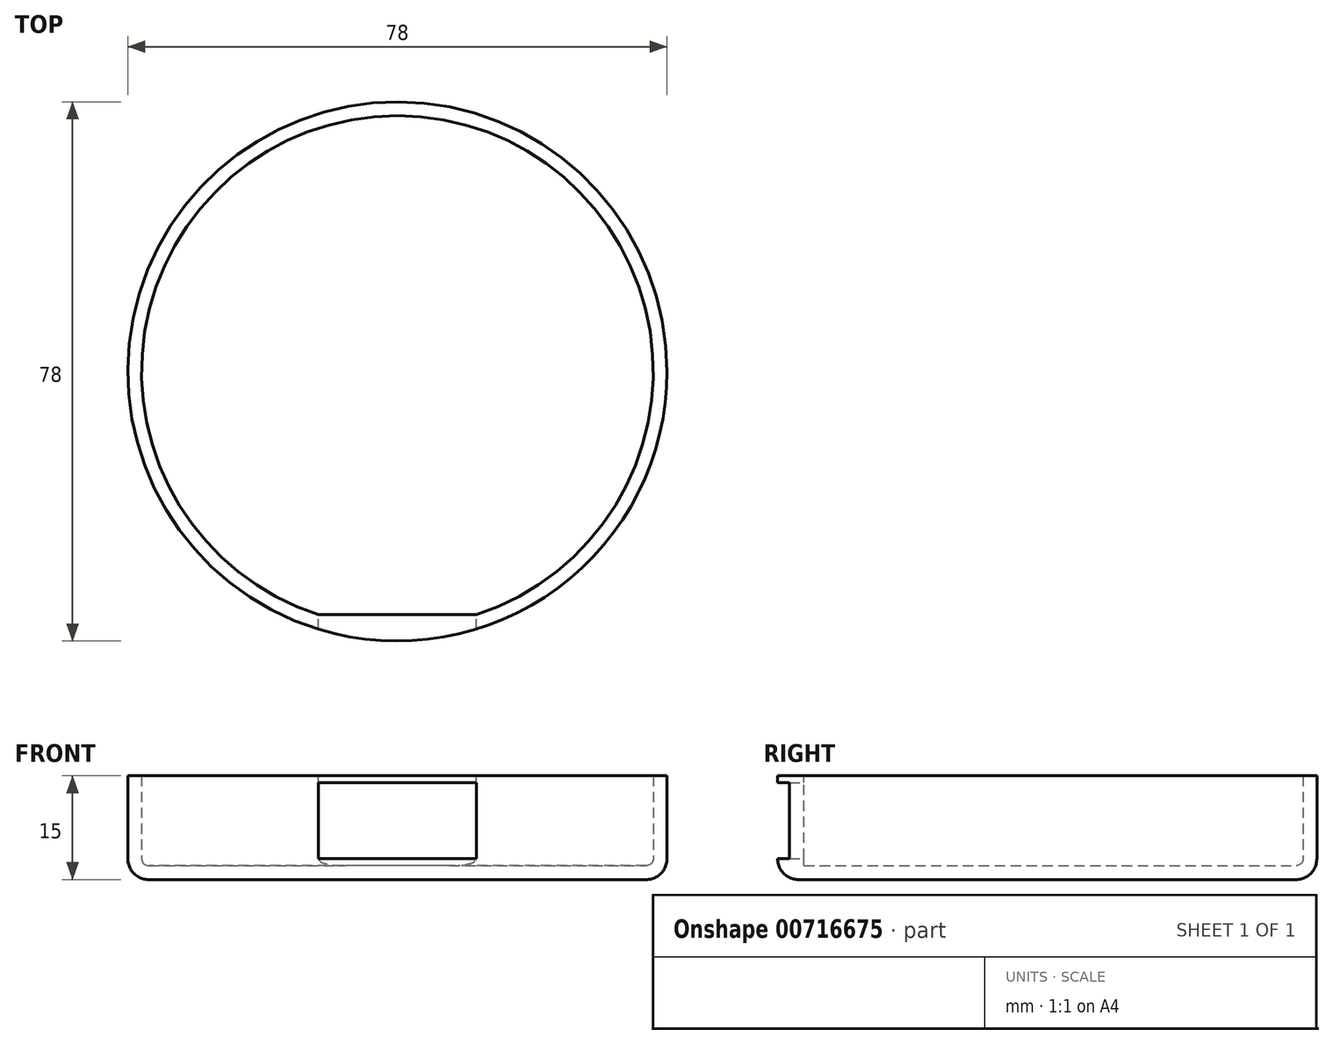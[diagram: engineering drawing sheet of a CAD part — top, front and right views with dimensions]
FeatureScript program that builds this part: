
annotation { "Feature Type Name" : "Feature", "Feature Type Description" : "" }
export const myFeature = defineFeature(function(context is Context, id is Id, definition is map)
    precondition{}
    {
        {
            var Q0;
            Q0=qCreatedBy(makeId("Top.planeOp"),FACE);
            var sketch = newSketch(context, id + "F0", { "sketchPlane" : qUnion([Q0])});
            skCircle(sketch, "E0", {"center": v(0, 0) * mm, "radius": 39 * mm});
            skSolve(sketch);
        }
        {
            var Q0;
            Q0 = qSketchRegion(id + "F0", true);
            extrude(context, id + "F1", {"entities" : qUnion([Q0]), "depth" : 15 * mm, "offsetDistance" : 25 * mm});
        }
        {
            var Q0;
            Q0=makeQuery(id+"F1.opExtrude","CAP_EDGE",EDGE,{"disambiguationData":[OSD([sQuery(id+"F0.wireOp",EDGE,"E0")])],"isStart":true});
            fillet(context, id + "F2", {"entities" : qUnion([Q0]), "radius" : 3 * mm, "tangentPropagation" : true, "allowEdgeOverflow" : false});
        }
        {
            var Q0;
            Q0=makeQuery(id+"F1.opExtrude","CAP_FACE",FACE,{"disambiguationData":[OSD([sQuery(id+"F0.wireOp",EDGE,"E0")])],"isStart":false});
            shell(context, id + "F3", {"entities" : qUnion([Q0]), "thickness" : 2 * mm});
        }
        {
            var Q0;
            Q0=makeQuery(id+"F1.opExtrude","CAP_FACE",FACE,{"disambiguationData":[OSD([sQuery(id+"F0.wireOp",EDGE,"E0")])],"isStart":false});
            var sketch = newSketch(context, id + "F4", { "sketchPlane" : qUnion([Q0])});
            skLineSegment(sketch, "E1", {"start": v(-11.4, -35.2) * mm, "end": v(11.4, -35.2) * mm});
            skArc(sketch, "E2", {"start": v(-11.4, -35.2) * mm, "mid": v(0, -37) * mm, "end": v(11.4, -35.2) * mm});
            skPoint(sketch, "E3", {"position": v(0, -39) * mm});
            skSolve(sketch);
        }
        {
            var Q0;
            Q0 = qSketchRegion(id + "F4", true);
            extrude(context, id + "F5", {"entities" : qUnion([Q0]), "operationType" : NewBodyOperationType.ADD, "endBound" : BoundingType.UP_TO_NEXT, "oppositeDirection" : true, "depth" : 25 * mm, "offsetDistance" : 25 * mm});
        }
        {
            var Q0;
            Q0=makeQuery(id+"F5.opExtrude","SWEPT_FACE",FACE,{"disambiguationData":[OSD([sQuery(id+"F4.wireOp",EDGE,"E1")])]});
            var sketch = newSketch(context, id + "F6", { "sketchPlane" : qUnion([Q0])});
            skLineSegment(sketch, "E4.bottom", {"start": v(-11.4, 14) * mm, "end": v(11.4, 14) * mm});
            skLineSegment(sketch, "E4.top", {"start": v(-11.4, 3) * mm, "end": v(11.4, 3) * mm});
            skLineSegment(sketch, "E4.left", {"start": v(-11.4, 14) * mm, "end": v(-11.4, 3) * mm});
            skLineSegment(sketch, "E4.right", {"start": v(11.4, 14) * mm, "end": v(11.4, 3) * mm});
            skSolve(sketch);
        }
        {
            var Q0;
            Q0 = qSketchRegion(id + "F6", true);
            extrude(context, id + "F7", {"entities" : qUnion([Q0]), "operationType" : NewBodyOperationType.REMOVE, "endBound" : BoundingType.THROUGH_ALL, "oppositeDirection" : true, "depth" : 25 * mm, "offsetDistance" : 25 * mm});
        }
    });
